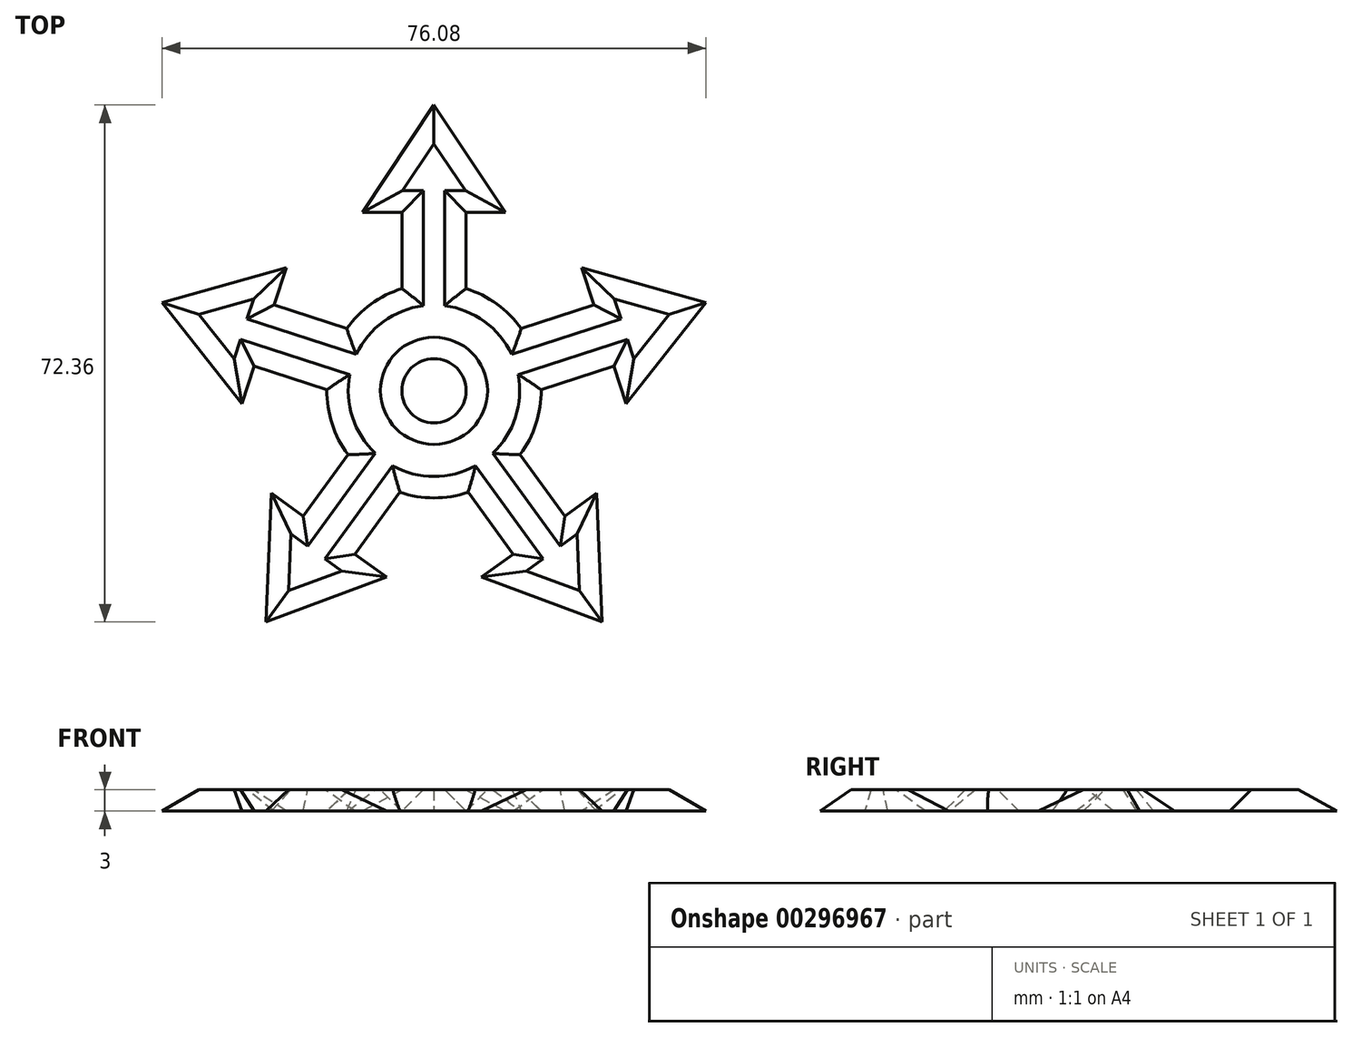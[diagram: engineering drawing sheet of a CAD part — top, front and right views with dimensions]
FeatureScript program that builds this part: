
annotation { "Feature Type Name" : "Feature", "Feature Type Description" : "" }
export const myFeature = defineFeature(function(context is Context, id is Id, definition is map)
    precondition{}
    {
        {
            var Q0;
            Q0=qCreatedBy(makeId("Top.planeOp"),FACE);
            var sketch = newSketch(context, id + "F0", { "sketchPlane" : qUnion([Q0])});
            skCircle(sketch, "E0", {"center": v(0, 0) * mm, "radius": 15 * mm});
            skLineSegment(sketch, "E1.bottom", {"start": v(-4.5, 8.84) * mm, "end": v(4.5, 8.84) * mm});
            skLineSegment(sketch, "E1.top", {"start": v(-4.5, 25) * mm, "end": v(4.5, 25) * mm});
            skLineSegment(sketch, "E1.left", {"start": v(-4.5, 8.84) * mm, "end": v(-4.5, 25) * mm});
            skLineSegment(sketch, "E1.right", {"start": v(4.5, 8.84) * mm, "end": v(4.5, 25) * mm});
            skLineSegment(sketch, "E2", {"start": v(0, 0) * mm, "end": v(0, 19.52) * mm, "construction": true});
            skPoint(sketch, "E3.endSnap0", {"position": v(0, 25) * mm});
            skLineSegment(sketch, "E4", {"start": v(-4.5, 25) * mm, "end": v(-10, 25) * mm});
            skLineSegment(sketch, "E5", {"start": v(-10, 25) * mm, "end": v(0, 40) * mm});
            skLineSegment(sketch, "E6", {"start": v(0, 40) * mm, "end": v(10, 25) * mm});
            skLineSegment(sketch, "E7", {"start": v(10, 25) * mm, "end": v(4.5, 25) * mm});
            skCircle(sketch, "E8", {"center": v(0, 0) * mm, "radius": 40 * mm, "construction": true});
            skLineSegment(sketch, "E9.1.0", {"start": v(-25.17, 3.45) * mm, "end": v(-26.87, -1.79) * mm});
            skLineSegment(sketch, "E9.1.1", {"start": v(-25.17, 3.45) * mm, "end": v(-22.39, 12) * mm});
            skLineSegment(sketch, "E9.1.2", {"start": v(-20.69, 17.24) * mm, "end": v(-22.39, 12) * mm});
            skLineSegment(sketch, "E9.1.3", {"start": v(-38.04, 12.36) * mm, "end": v(-20.69, 17.24) * mm});
            skLineSegment(sketch, "E9.1.4", {"start": v(-26.87, -1.79) * mm, "end": v(-38.04, 12.36) * mm});
            skLineSegment(sketch, "E9.1.5", {"start": v(-9.8, -1.55) * mm, "end": v(-25.17, 3.45) * mm});
            skLineSegment(sketch, "E9.1.6", {"start": v(-7.01, 7.01) * mm, "end": v(-22.39, 12) * mm});
            skLineSegment(sketch, "E9.1.7", {"start": v(-9.8, -1.55) * mm, "end": v(-7.01, 7.01) * mm});
            skLineSegment(sketch, "E9.2.0", {"start": v(-11.05, -22.87) * mm, "end": v(-6.6, -26.1) * mm});
            skLineSegment(sketch, "E9.2.1", {"start": v(-11.05, -22.87) * mm, "end": v(-18.34, -17.58) * mm});
            skLineSegment(sketch, "E9.2.2", {"start": v(-22.78, -14.35) * mm, "end": v(-18.34, -17.58) * mm});
            skLineSegment(sketch, "E9.2.3", {"start": v(-23.51, -32.36) * mm, "end": v(-22.78, -14.35) * mm});
            skLineSegment(sketch, "E9.2.4", {"start": v(-6.6, -26.1) * mm, "end": v(-23.51, -32.36) * mm});
            skLineSegment(sketch, "E9.2.5", {"start": v(-1.55, -9.8) * mm, "end": v(-11.05, -22.87) * mm});
            skLineSegment(sketch, "E9.2.6", {"start": v(-8.83, -4.5) * mm, "end": v(-18.34, -17.58) * mm});
            skLineSegment(sketch, "E9.2.7", {"start": v(-1.55, -9.8) * mm, "end": v(-8.83, -4.5) * mm});
            skLineSegment(sketch, "E9.3.0", {"start": v(18.34, -17.58) * mm, "end": v(22.78, -14.35) * mm});
            skLineSegment(sketch, "E9.3.1", {"start": v(18.34, -17.58) * mm, "end": v(11.05, -22.87) * mm});
            skLineSegment(sketch, "E9.3.2", {"start": v(6.6, -26.1) * mm, "end": v(11.05, -22.87) * mm});
            skLineSegment(sketch, "E9.3.3", {"start": v(23.51, -32.36) * mm, "end": v(6.6, -26.1) * mm});
            skLineSegment(sketch, "E9.3.4", {"start": v(22.78, -14.35) * mm, "end": v(23.51, -32.36) * mm});
            skLineSegment(sketch, "E9.3.5", {"start": v(8.83, -4.5) * mm, "end": v(18.34, -17.58) * mm});
            skLineSegment(sketch, "E9.3.6", {"start": v(1.55, -9.8) * mm, "end": v(11.05, -22.87) * mm});
            skLineSegment(sketch, "E9.3.7", {"start": v(8.83, -4.5) * mm, "end": v(1.55, -9.8) * mm});
            skLineSegment(sketch, "E9.4.0", {"start": v(22.39, 12) * mm, "end": v(20.69, 17.24) * mm});
            skLineSegment(sketch, "E9.4.1", {"start": v(22.39, 12) * mm, "end": v(25.17, 3.45) * mm});
            skLineSegment(sketch, "E9.4.2", {"start": v(26.87, -1.79) * mm, "end": v(25.17, 3.45) * mm});
            skLineSegment(sketch, "E9.4.3", {"start": v(38.04, 12.36) * mm, "end": v(26.87, -1.79) * mm});
            skLineSegment(sketch, "E9.4.4", {"start": v(20.69, 17.24) * mm, "end": v(38.04, 12.36) * mm});
            skLineSegment(sketch, "E9.4.5", {"start": v(7.01, 7.01) * mm, "end": v(22.39, 12) * mm});
            skLineSegment(sketch, "E9.4.6", {"start": v(9.8, -1.55) * mm, "end": v(25.17, 3.45) * mm});
            skLineSegment(sketch, "E9.4.7", {"start": v(7.01, 7.01) * mm, "end": v(9.8, -1.55) * mm});
            skCircle(sketch, "E10", {"center": v(0, 0) * mm, "radius": 4.5 * mm});
            skSolve(sketch);
        }
        {
            var Q0;
            Q0 = qSketchRegion(id + "F0", true);
            extrude(context, id + "F1", {"entities" : qUnion([Q0]), "depth" : 3 * mm});
        }
        {
            var Q0;
            Q0=makeQuery(id+"F1.opExtrude","CAP_FACE",FACE,{"disambiguationData":[OSD([sQuery(id+"F0.wireOp",EDGE,"E0"),sQuery(id+"F0.wireOp",EDGE,"E1.left"),sQuery(id+"F0.wireOp",EDGE,"E1.right"),sQuery(id+"F0.wireOp",EDGE,"E4"),sQuery(id+"F0.wireOp",EDGE,"E5"),sQuery(id+"F0.wireOp",EDGE,"E6"),sQuery(id+"F0.wireOp",EDGE,"E7"),sQuery(id+"F0.wireOp",EDGE,"E9.1.0"),sQuery(id+"F0.wireOp",EDGE,"E9.1.2"),sQuery(id+"F0.wireOp",EDGE,"E9.1.3"),sQuery(id+"F0.wireOp",EDGE,"E9.1.4"),sQuery(id+"F0.wireOp",EDGE,"E9.1.5"),sQuery(id+"F0.wireOp",EDGE,"E9.1.6"),sQuery(id+"F0.wireOp",EDGE,"E9.2.0"),sQuery(id+"F0.wireOp",EDGE,"E9.2.2"),sQuery(id+"F0.wireOp",EDGE,"E9.2.3"),sQuery(id+"F0.wireOp",EDGE,"E9.2.4"),sQuery(id+"F0.wireOp",EDGE,"E9.2.5"),sQuery(id+"F0.wireOp",EDGE,"E9.2.6"),sQuery(id+"F0.wireOp",EDGE,"E9.3.0"),sQuery(id+"F0.wireOp",EDGE,"E9.3.2"),sQuery(id+"F0.wireOp",EDGE,"E9.3.3"),sQuery(id+"F0.wireOp",EDGE,"E9.3.4"),sQuery(id+"F0.wireOp",EDGE,"E9.3.5"),sQuery(id+"F0.wireOp",EDGE,"E9.3.6"),sQuery(id+"F0.wireOp",EDGE,"E9.4.0"),sQuery(id+"F0.wireOp",EDGE,"E9.4.2"),sQuery(id+"F0.wireOp",EDGE,"E9.4.3"),sQuery(id+"F0.wireOp",EDGE,"E9.4.4"),sQuery(id+"F0.wireOp",EDGE,"E9.4.5"),sQuery(id+"F0.wireOp",EDGE,"E9.4.6"),sQuery(id+"F0.wireOp",EDGE,"E10")])],"isStart":false});
            chamfer(context, id + "F2", {"entities" : qUnion([Q0]), "chamferType" : ChamferType.TWO_OFFSETS, "width1" : 3 * mm, "oppositeDirection" : true, "width2" : 3 * mm, "tangentPropagation" : true});
        }
    });
